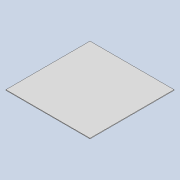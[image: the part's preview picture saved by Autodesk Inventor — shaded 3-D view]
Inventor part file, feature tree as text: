
AUTODESK INVENTOR PART (.ipt)
format: ipt  version: 2020 (Build 240168000, 168)  size: 72,704 bytes
history: native  units: mm
features: extrude x1, sketch x1
ambient origin geometry x8: Origin, YZ Plane, XZ Plane, XY Plane, X Axis, Y Axis, Z Axis, Center Point
bodies: Solid1 (feature_tree)
feature tree (2):
  extrude  "Extrusion1"  Depth=40.0mm
  sketch  "Sketch1"  dims[d0=40.0mm d1=40.0mm d2=0.3mm d3=0.0mm]
